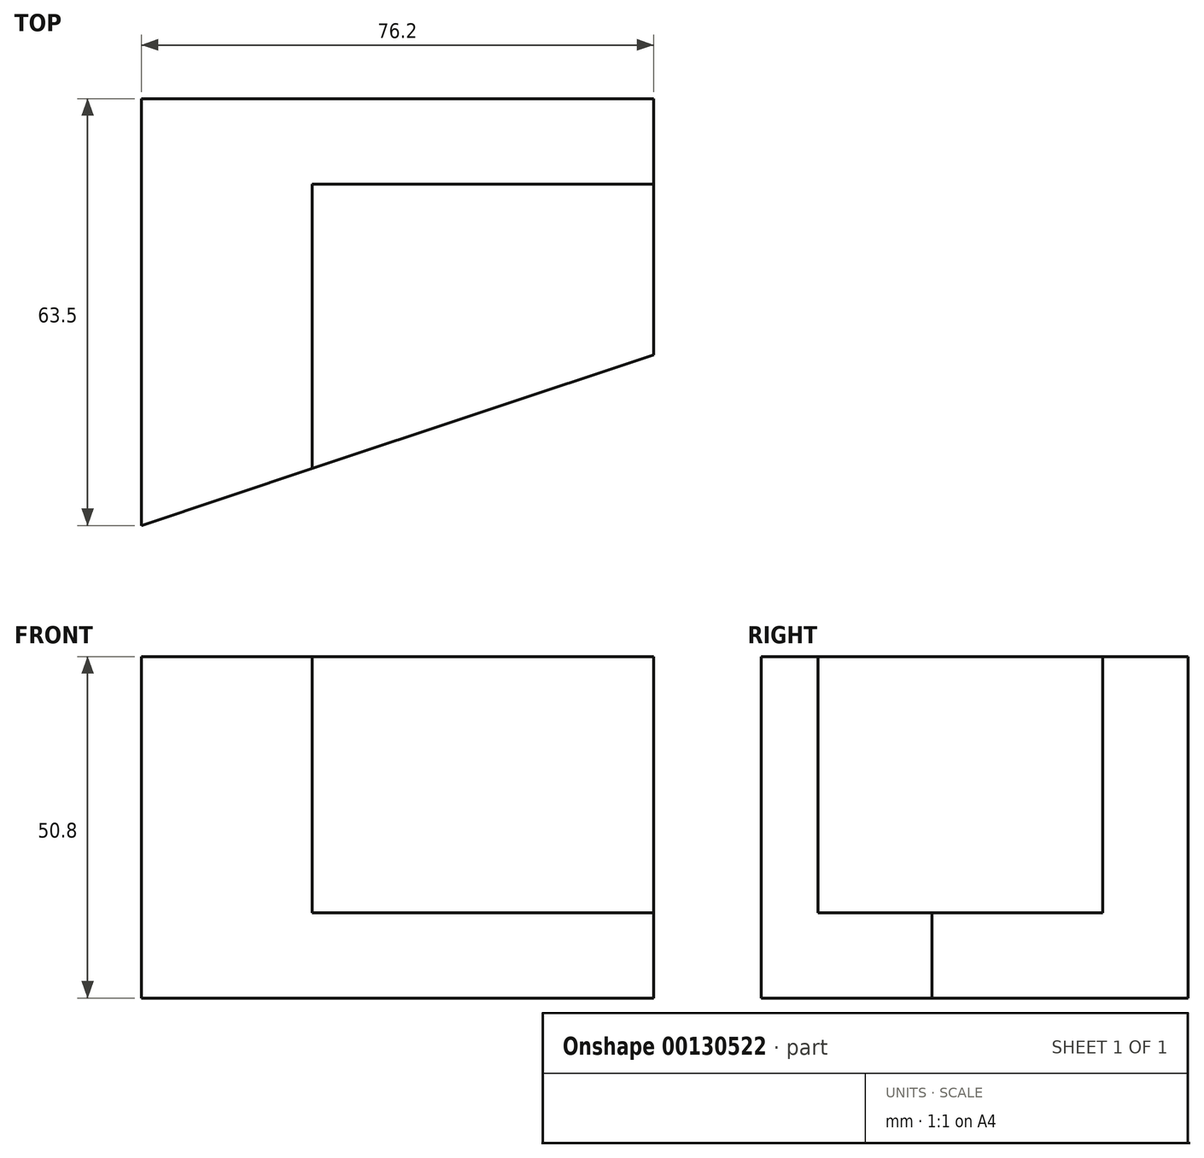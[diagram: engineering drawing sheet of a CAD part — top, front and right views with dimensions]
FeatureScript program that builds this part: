
annotation { "Feature Type Name" : "Feature", "Feature Type Description" : "" }
export const myFeature = defineFeature(function(context is Context, id is Id, definition is map)
    precondition{}
    {
        {
            var Q0;
            Q0=qCreatedBy(makeId("Front.planeOp"),FACE);
            var sketch = newSketch(context, id + "F0", { "sketchPlane" : qUnion([Q0])});
            skLineSegment(sketch, "E0", {"start": v(0, 0) * mm, "end": v(0, 50.8) * mm});
            skLineSegment(sketch, "E1", {"start": v(0, 50.8) * mm, "end": v(25.4, 50.8) * mm});
            skLineSegment(sketch, "E2", {"start": v(25.4, 50.8) * mm, "end": v(25.4, 12.7) * mm});
            skLineSegment(sketch, "E3", {"start": v(25.4, 12.7) * mm, "end": v(76.2, 12.7) * mm});
            skLineSegment(sketch, "E4", {"start": v(76.2, 12.7) * mm, "end": v(76.2, 0) * mm});
            skLineSegment(sketch, "E5", {"start": v(76.2, 0) * mm, "end": v(0, 0) * mm});
            skSolve(sketch);
        }
        {
            var Q0;
            Q0 = qSketchRegion(id + "F0", true);
            extrude(context, id + "F1", {"entities" : qUnion([Q0]), "depth" : 63.5 * mm});
        }
        {
            var Q0;
            Q0=qCreatedBy(makeId("Front.planeOp"),FACE);
            var sketch = newSketch(context, id + "F2", { "sketchPlane" : qUnion([Q0])});
            skLineSegment(sketch, "E6.bottom", {"start": v(0, 0) * mm, "end": v(76.2, 0) * mm});
            skLineSegment(sketch, "E6.top", {"start": v(0, 50.8) * mm, "end": v(76.2, 50.8) * mm});
            skLineSegment(sketch, "E6.left", {"start": v(0, 0) * mm, "end": v(0, 50.8) * mm});
            skLineSegment(sketch, "E6.right", {"start": v(76.2, 0) * mm, "end": v(76.2, 50.8) * mm});
            skSolve(sketch);
        }
        {
            var Q0;
            Q0 = qSketchRegion(id + "F2", true);
            extrude(context, id + "F3", {"entities" : qUnion([Q0]), "operationType" : NewBodyOperationType.ADD, "depth" : 12.7 * mm});
        }
        {
            var Q0;
            Q0=qCreatedBy(makeId("Top.planeOp"),FACE);
            var sketch = newSketch(context, id + "F4", { "sketchPlane" : qUnion([Q0])});
            skLineSegment(sketch, "E7", {"start": v(0, -63.5) * mm, "end": v(76.2, -63.5) * mm});
            skLineSegment(sketch, "E8", {"start": v(76.2, -63.5) * mm, "end": v(76.2, -38.1) * mm});
            skLineSegment(sketch, "E9", {"start": v(76.2, -38.1) * mm, "end": v(0, -63.5) * mm});
            skSolve(sketch);
        }
        {
            var Q0;
            Q0 = qSketchRegion(id + "F4", true);
            extrude(context, id + "F5", {"entities" : qUnion([Q0]), "operationType" : NewBodyOperationType.REMOVE, "depth" : 50.8 * mm});
        }
    });
